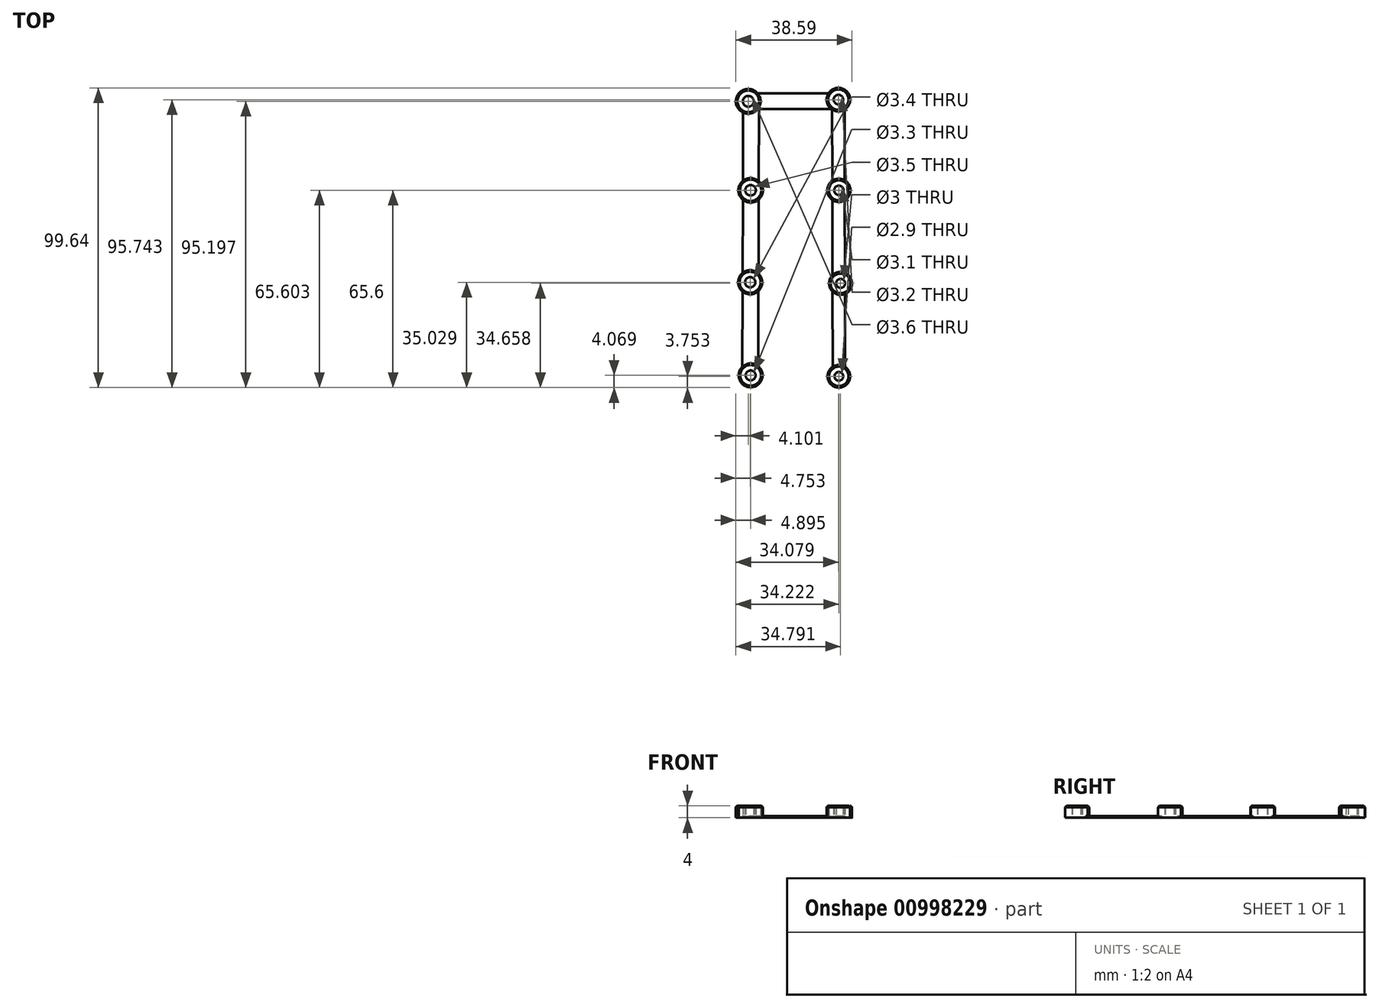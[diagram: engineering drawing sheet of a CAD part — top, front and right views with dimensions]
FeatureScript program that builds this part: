
annotation { "Feature Type Name" : "Feature", "Feature Type Description" : "" }
export const myFeature = defineFeature(function(context is Context, id is Id, definition is map)
    precondition{}
    {
        {
            var Q0;
            Q0=qCreatedBy(makeId("Top.planeOp"),FACE);
            var sketch = newSketch(context, id + "F0", { "sketchPlane" : qUnion([Q0])});
            skCircle(sketch, "E0", {"center": v(-37.62, 22.58) * mm, "radius": 4.1 * mm});
            skCircle(sketch, "E1", {"center": v(-36.82, -7.02) * mm, "radius": 4.05 * mm});
            skCircle(sketch, "E2", {"center": v(-36.97, -37.6) * mm, "radius": 4 * mm});
            skCircle(sketch, "E3", {"center": v(-36.83, -68.55) * mm, "radius": 3.95 * mm});
            skCircle(sketch, "E4", {"center": v(-7.64, 23.12) * mm, "radius": 3.9 * mm});
            skCircle(sketch, "E5", {"center": v(-7.5, -7.02) * mm, "radius": 3.85 * mm});
            skCircle(sketch, "E6", {"center": v(-6.93, -37.96) * mm, "radius": 3.8 * mm});
            skCircle(sketch, "E7", {"center": v(-7.5, -68.87) * mm, "radius": 3.75 * mm});
            skCircle(sketch, "E8", {"center": v(-37.62, 22.58) * mm, "radius": 1.8 * mm});
            skCircle(sketch, "E9", {"center": v(-36.82, -7.02) * mm, "radius": 1.75 * mm});
            skCircle(sketch, "E10", {"center": v(-36.97, -37.6) * mm, "radius": 1.7 * mm});
            skCircle(sketch, "E11", {"center": v(-36.83, -68.55) * mm, "radius": 1.65 * mm});
            skCircle(sketch, "E12", {"center": v(-7.64, 23.12) * mm, "radius": 1.6 * mm});
            skCircle(sketch, "E13", {"center": v(-7.5, -7.02) * mm, "radius": 1.55 * mm});
            skCircle(sketch, "E14", {"center": v(-6.93, -37.96) * mm, "radius": 1.5 * mm});
            skCircle(sketch, "E15", {"center": v(-7.5, -68.87) * mm, "radius": 1.45 * mm});
            skLineSegment(sketch, "E16.left", {"start": v(-39.32, 18.84) * mm, "end": v(-39.39, -3.88) * mm});
            skLineSegment(sketch, "E16.right", {"start": v(-34.03, 20.02) * mm, "end": v(-34.1, -4.01) * mm});
            skLineSegment(sketch, "E17.left", {"start": v(-9.72, 19.82) * mm, "end": v(-9.68, -3.85) * mm});
            skLineSegment(sketch, "E17.right", {"start": v(-5.6, 19.8) * mm, "end": v(-5.56, -3.7) * mm});
            skPoint(sketch, "E18.orphan", {"position": v(-34.33, -75.74) * mm});
            skPoint(sketch, "E19.orphan", {"position": v(-5.43, -75.74) * mm});
            skLineSegment(sketch, "E20.trimOffspring", {"start": v(-34.03, 20.02) * mm, "end": v(-10, 20.02) * mm});
            skLineSegment(sketch, "E21.trimOffspring", {"start": v(-34.45, 25.17) * mm, "end": v(-10.96, 25.17) * mm});
            skLineSegment(sketch, "E22.trimOffspring", {"start": v(-39.4, -10.14) * mm, "end": v(-39.48, -34.48) * mm});
            skLineSegment(sketch, "E23.trimOffspring", {"start": v(-34.13, -10.04) * mm, "end": v(-34.2, -34.7) * mm});
            skLineSegment(sketch, "E24.trimOffspring", {"start": v(-9.67, -10.2) * mm, "end": v(-9.62, -35.28) * mm});
            skLineSegment(sketch, "E25.trimOffspring", {"start": v(-5.54, -10.34) * mm, "end": v(-5.5, -34.44) * mm});
            skLineSegment(sketch, "E26.trimOffspring", {"start": v(-39.5, -40.69) * mm, "end": v(-39.58, -65.72) * mm});
            skLineSegment(sketch, "E27.trimOffspring", {"start": v(-34.22, -40.5) * mm, "end": v(-34.3, -65.52) * mm});
            skLineSegment(sketch, "E28.trimOffspring", {"start": v(-5.49, -41.48) * mm, "end": v(-5.45, -65.73) * mm});
            skLineSegment(sketch, "E29.trimOffspring", {"start": v(-9.61, -40.65) * mm, "end": v(-9.57, -65.74) * mm});
            skSolve(sketch);
        }
        {
            var Q0;
            Q0=makeQuery(id+"F0.imprint","IMPRINT",FACE,{"disambiguationData":[TD([[makeQuery(id+"F0.imprint","IMPRINT",EDGE,{"derivedFrom":sQuery(id+"F0.wireOp",EDGE,"E0")}),-1.0]])]});
            var Q1;
            {var subQ0=sQuery(id+"F0.wireOp",EDGE,"E16.left");var subQ1=sQuery(id+"F0.wireOp",EDGE,"E1");var subQ2=makeQuery(id+"F0.imprint","INTERSECT",VERTEX,{"disambiguationData":[OD(1.0)],"derivedFrom":[subQ1,subQ0]});Q1=makeQuery(id+"F0.imprint","IMPRINT",FACE,{"disambiguationData":[TD([[makeQuery(id+"F0.imprint","IMPRINT",EDGE,{"disambiguationData":[TD([[subQ2,-1.0]])],"derivedFrom":subQ1}),-1.0]])]});}
            var Q2;
            {var subQ0=sQuery(id+"F0.wireOp",EDGE,"E16.left");var subQ1=sQuery(id+"F0.wireOp",EDGE,"E2");var subQ2=makeQuery(id+"F0.imprint","INTERSECT",VERTEX,{"disambiguationData":[OD(1.0)],"derivedFrom":[subQ1,subQ0]});Q2=makeQuery(id+"F0.imprint","IMPRINT",FACE,{"disambiguationData":[TD([[makeQuery(id+"F0.imprint","IMPRINT",EDGE,{"disambiguationData":[TD([[subQ2,-1.0]])],"derivedFrom":subQ1}),-1.0]])]});}
            var Q3;
            {var subQ0=sQuery(id+"F0.wireOp",EDGE,"E17.left");var subQ1=sQuery(id+"F0.wireOp",EDGE,"E5");var subQ2=makeQuery(id+"F0.imprint","INTERSECT",VERTEX,{"disambiguationData":[OD(1.0)],"derivedFrom":[subQ1,subQ0]});Q3=makeQuery(id+"F0.imprint","IMPRINT",FACE,{"disambiguationData":[TD([[makeQuery(id+"F0.imprint","IMPRINT",EDGE,{"disambiguationData":[TD([[subQ2,-1.0]])],"derivedFrom":subQ1}),-1.0]])]});}
            var Q4;
            {var subQ0=sQuery(id+"F0.wireOp",EDGE,"E17.left");var subQ1=sQuery(id+"F0.wireOp",EDGE,"E6");var subQ2=makeQuery(id+"F0.imprint","INTERSECT",VERTEX,{"disambiguationData":[OD(1.0)],"derivedFrom":[subQ1,subQ0]});Q4=makeQuery(id+"F0.imprint","IMPRINT",FACE,{"disambiguationData":[TD([[makeQuery(id+"F0.imprint","IMPRINT",EDGE,{"disambiguationData":[TD([[subQ2,-1.0]])],"derivedFrom":subQ1}),-1.0]])]});}
            var Q5;
            {var subQ0=sQuery(id+"F0.wireOp",EDGE,"E16.left");var subQ5=sQuery(id+"F0.wireOp",EDGE,"E0");var subQ6=makeQuery(id+"F0.imprint","INTERSECT",VERTEX,{"derivedFrom":[subQ5,subQ0]});Q5=makeQuery(id+"F0.imprint","IMPRINT",FACE,{"disambiguationData":[TD([[makeQuery(id+"F0.imprint","IMPRINT",EDGE,{"disambiguationData":[TD([[subQ6,-1.0]])],"derivedFrom":subQ5}),-1.0]])]});}
            var Q6;
            {var subQ5=sQuery(id+"F0.wireOp",EDGE,"kUI5SBMI-iPfT-wOSN-fbtu-PMcIkSxUXb8U.left");Q6=makeQuery(id+"F0.imprint","IMPRINT",FACE,{"disambiguationData":[TD([[makeQuery(id+"F0.imprint","IMPRINT",EDGE,{"derivedFrom":subQ5}),1.0]])]});}
            var Q7;
            {var subQ0=sQuery(id+"F0.wireOp",EDGE,"kUI5SBMI-iPfT-wOSN-fbtu-PMcIkSxUXb8U.bottom");var subQ3=sQuery(id+"F0.wireOp",EDGE,"E4");var subQ4=makeQuery(id+"F0.imprint","INTERSECT",VERTEX,{"disambiguationData":[OD(0.0)],"derivedFrom":[subQ3,subQ0]});Q7=makeQuery(id+"F0.imprint","IMPRINT",FACE,{"disambiguationData":[TD([[makeQuery(id+"F0.imprint","IMPRINT",EDGE,{"disambiguationData":[TD([[subQ4,-1.0]])],"derivedFrom":subQ3}),-1.0]])]});}
            var Q8;
            {var subQ5=sQuery(id+"F0.wireOp",EDGE,"kUI5SBMI-iPfT-wOSN-fbtu-PMcIkSxUXb8U.right");Q8=makeQuery(id+"F0.imprint","IMPRINT",FACE,{"disambiguationData":[TD([[makeQuery(id+"F0.imprint","IMPRINT",EDGE,{"derivedFrom":subQ5}),-1.0]])]});}
            var Q9;
            {var subQ0=sQuery(id+"F0.wireOp",EDGE,"E17.left");var subQ1=sQuery(id+"F0.wireOp",EDGE,"E4");var subQ2=makeQuery(id+"F0.imprint","INTERSECT",VERTEX,{"derivedFrom":[subQ1,subQ0]});Q9=makeQuery(id+"F0.imprint","IMPRINT",FACE,{"disambiguationData":[TD([[makeQuery(id+"F0.imprint","IMPRINT",EDGE,{"disambiguationData":[TD([[subQ2,-1.0]])],"derivedFrom":subQ1}),-1.0]])]});}
            extrude(context, id + "F1", {"entities" : qUnion([Q0, Q1, Q2, Q3, Q4, Q5, Q6, Q7, Q8, Q9]), "depth" : .5 * mm, "offsetDistance" : 25 * mm});
        }
        {
            var Q0;
            Q0=makeQuery(id+"F0.imprint","IMPRINT",FACE,{"disambiguationData":[TD([[makeQuery(id+"F0.imprint","IMPRINT",EDGE,{"derivedFrom":sQuery(id+"F0.wireOp",EDGE,"E0")}),1.0]])]});
            var Q1;
            Q1=makeQuery(id+"F0.imprint","IMPRINT",FACE,{"disambiguationData":[TD([[makeQuery(id+"F0.imprint","IMPRINT",EDGE,{"derivedFrom":sQuery(id+"F0.wireOp",EDGE,"E1")}),1.0]])]});
            var Q2;
            Q2=makeQuery(id+"F0.imprint","IMPRINT",FACE,{"disambiguationData":[TD([[makeQuery(id+"F0.imprint","IMPRINT",EDGE,{"derivedFrom":sQuery(id+"F0.wireOp",EDGE,"E2")}),1.0]])]});
            var Q3;
            Q3=makeQuery(id+"F0.imprint","IMPRINT",FACE,{"disambiguationData":[TD([[makeQuery(id+"F0.imprint","IMPRINT",EDGE,{"derivedFrom":sQuery(id+"F0.wireOp",EDGE,"E3")}),1.0]])]});
            var Q4;
            Q4=makeQuery(id+"F0.imprint","IMPRINT",FACE,{"disambiguationData":[TD([[makeQuery(id+"F0.imprint","IMPRINT",EDGE,{"derivedFrom":sQuery(id+"F0.wireOp",EDGE,"E7")}),1.0]])]});
            var Q5;
            Q5=makeQuery(id+"F0.imprint","IMPRINT",FACE,{"disambiguationData":[TD([[makeQuery(id+"F0.imprint","IMPRINT",EDGE,{"derivedFrom":sQuery(id+"F0.wireOp",EDGE,"E6")}),1.0]])]});
            var Q6;
            Q6=makeQuery(id+"F0.imprint","IMPRINT",FACE,{"disambiguationData":[TD([[makeQuery(id+"F0.imprint","IMPRINT",EDGE,{"derivedFrom":sQuery(id+"F0.wireOp",EDGE,"E5")}),1.0]])]});
            var Q7;
            Q7=makeQuery(id+"F0.imprint","IMPRINT",FACE,{"disambiguationData":[TD([[makeQuery(id+"F0.imprint","IMPRINT",EDGE,{"derivedFrom":sQuery(id+"F0.wireOp",EDGE,"E4")}),1.0]])]});
            var Q8;
            {var subQ0=sQuery(id+"F0.wireOp",EDGE,"E16.left");var subQ1=sQuery(id+"F0.wireOp",EDGE,"E1");var subQ2=makeQuery(id+"F0.imprint","INTERSECT",VERTEX,{"disambiguationData":[OD(0.0)],"derivedFrom":[subQ1,subQ0]});Q8=makeQuery(id+"F0.imprint","IMPRINT",FACE,{"disambiguationData":[TD([[makeQuery(id+"F0.imprint","IMPRINT",EDGE,{"disambiguationData":[TD([[subQ2,-1.0]])],"derivedFrom":subQ1}),1.0]])]});}
            var Q9;
            {var subQ0=sQuery(id+"F0.wireOp",EDGE,"E16.right");var subQ1=sQuery(id+"F0.wireOp",EDGE,"E1");var subQ2=makeQuery(id+"F0.imprint","INTERSECT",VERTEX,{"disambiguationData":[OD(0.0)],"derivedFrom":[subQ1,subQ0]});Q9=makeQuery(id+"F0.imprint","IMPRINT",FACE,{"disambiguationData":[TD([[makeQuery(id+"F0.imprint","IMPRINT",EDGE,{"disambiguationData":[TD([[subQ2,1.0]])],"derivedFrom":subQ1}),1.0]])]});}
            var Q10;
            {var subQ0=sQuery(id+"F0.wireOp",EDGE,"E16.left");var subQ1=sQuery(id+"F0.wireOp",EDGE,"E2");var subQ2=makeQuery(id+"F0.imprint","INTERSECT",VERTEX,{"disambiguationData":[OD(0.0)],"derivedFrom":[subQ1,subQ0]});Q10=makeQuery(id+"F0.imprint","IMPRINT",FACE,{"disambiguationData":[TD([[makeQuery(id+"F0.imprint","IMPRINT",EDGE,{"disambiguationData":[TD([[subQ2,-1.0]])],"derivedFrom":subQ1}),1.0]])]});}
            var Q11;
            {var subQ0=sQuery(id+"F0.wireOp",EDGE,"E16.right");var subQ1=sQuery(id+"F0.wireOp",EDGE,"E2");var subQ2=makeQuery(id+"F0.imprint","INTERSECT",VERTEX,{"disambiguationData":[OD(0.0)],"derivedFrom":[subQ1,subQ0]});Q11=makeQuery(id+"F0.imprint","IMPRINT",FACE,{"disambiguationData":[TD([[makeQuery(id+"F0.imprint","IMPRINT",EDGE,{"disambiguationData":[TD([[subQ2,1.0]])],"derivedFrom":subQ1}),1.0]])]});}
            var Q12;
            {var subQ0=sQuery(id+"F0.wireOp",EDGE,"E17.left");var subQ1=sQuery(id+"F0.wireOp",EDGE,"E5");var subQ2=makeQuery(id+"F0.imprint","INTERSECT",VERTEX,{"disambiguationData":[OD(0.0)],"derivedFrom":[subQ1,subQ0]});Q12=makeQuery(id+"F0.imprint","IMPRINT",FACE,{"disambiguationData":[TD([[makeQuery(id+"F0.imprint","IMPRINT",EDGE,{"disambiguationData":[TD([[subQ2,-1.0]])],"derivedFrom":subQ1}),1.0]])]});}
            var Q13;
            {var subQ0=sQuery(id+"F0.wireOp",EDGE,"E17.right");var subQ1=sQuery(id+"F0.wireOp",EDGE,"E5");var subQ2=makeQuery(id+"F0.imprint","INTERSECT",VERTEX,{"disambiguationData":[OD(0.0)],"derivedFrom":[subQ1,subQ0]});Q13=makeQuery(id+"F0.imprint","IMPRINT",FACE,{"disambiguationData":[TD([[makeQuery(id+"F0.imprint","IMPRINT",EDGE,{"disambiguationData":[TD([[subQ2,1.0]])],"derivedFrom":subQ1}),1.0]])]});}
            var Q14;
            {var subQ0=sQuery(id+"F0.wireOp",EDGE,"E17.left");var subQ1=sQuery(id+"F0.wireOp",EDGE,"E6");var subQ2=makeQuery(id+"F0.imprint","INTERSECT",VERTEX,{"disambiguationData":[OD(0.0)],"derivedFrom":[subQ1,subQ0]});Q14=makeQuery(id+"F0.imprint","IMPRINT",FACE,{"disambiguationData":[TD([[makeQuery(id+"F0.imprint","IMPRINT",EDGE,{"disambiguationData":[TD([[subQ2,-1.0]])],"derivedFrom":subQ1}),1.0]])]});}
            var Q15;
            {var subQ0=sQuery(id+"F0.wireOp",EDGE,"E17.right");var subQ1=sQuery(id+"F0.wireOp",EDGE,"E6");var subQ2=makeQuery(id+"F0.imprint","INTERSECT",VERTEX,{"disambiguationData":[OD(0.0)],"derivedFrom":[subQ1,subQ0]});Q15=makeQuery(id+"F0.imprint","IMPRINT",FACE,{"disambiguationData":[TD([[makeQuery(id+"F0.imprint","IMPRINT",EDGE,{"disambiguationData":[TD([[subQ2,1.0]])],"derivedFrom":subQ1}),1.0]])]});}
            var Q16;
            {var subQ0=sQuery(id+"F0.wireOp",EDGE,"E16.right");var subQ1=sQuery(id+"F0.wireOp",EDGE,"E3");var subQ2=makeQuery(id+"F0.imprint","INTERSECT",VERTEX,{"disambiguationData":[OD(0.0)],"derivedFrom":[subQ1,subQ0]});Q16=makeQuery(id+"F0.imprint","IMPRINT",FACE,{"disambiguationData":[TD([[makeQuery(id+"F0.imprint","IMPRINT",EDGE,{"disambiguationData":[TD([[subQ2,-1.0]])],"derivedFrom":subQ1}),1.0]])]});}
            var Q17;
            {var subQ0=sQuery(id+"F0.wireOp",EDGE,"E16.left");var subQ1=sQuery(id+"F0.wireOp",EDGE,"E3");var subQ2=makeQuery(id+"F0.imprint","INTERSECT",VERTEX,{"disambiguationData":[OD(0.0)],"derivedFrom":[subQ1,subQ0]});Q17=makeQuery(id+"F0.imprint","IMPRINT",FACE,{"disambiguationData":[TD([[makeQuery(id+"F0.imprint","IMPRINT",EDGE,{"disambiguationData":[TD([[subQ2,1.0]])],"derivedFrom":subQ1}),1.0]])]});}
            var Q18;
            {var subQ0=sQuery(id+"F0.wireOp",EDGE,"E17.left");var subQ1=sQuery(id+"F0.wireOp",EDGE,"E7");var subQ2=makeQuery(id+"F0.imprint","INTERSECT",VERTEX,{"disambiguationData":[OD(0.0)],"derivedFrom":[subQ1,subQ0]});Q18=makeQuery(id+"F0.imprint","IMPRINT",FACE,{"disambiguationData":[TD([[makeQuery(id+"F0.imprint","IMPRINT",EDGE,{"disambiguationData":[TD([[subQ2,1.0]])],"derivedFrom":subQ1}),1.0]])]});}
            var Q19;
            {var subQ0=sQuery(id+"F0.wireOp",EDGE,"E17.right");var subQ1=sQuery(id+"F0.wireOp",EDGE,"E7");var subQ2=makeQuery(id+"F0.imprint","INTERSECT",VERTEX,{"disambiguationData":[OD(0.0)],"derivedFrom":[subQ1,subQ0]});Q19=makeQuery(id+"F0.imprint","IMPRINT",FACE,{"disambiguationData":[TD([[makeQuery(id+"F0.imprint","IMPRINT",EDGE,{"disambiguationData":[TD([[subQ2,-1.0]])],"derivedFrom":subQ1}),1.0]])]});}
            extrude(context, id + "F2", {"entities" : qUnion([Q0, Q1, Q2, Q3, Q4, Q5, Q6, Q7, Q8, Q9, Q10, Q11, Q12, Q13, Q14, Q15, Q16, Q17, Q18, Q19]), "operationType" : NewBodyOperationType.ADD, "depth" : 4 * mm, "offsetDistance" : 25 * mm});
        }
        {
            var Q0;
            Q0=makeQuery(id+"F2.opExtrude","CAP_EDGE",EDGE,{"disambiguationData":[OSD([sQuery(id+"F0.wireOp",EDGE,"E0")])],"isStart":false});
            var Q1;
            Q1=makeQuery(id+"F2.opExtrude","CAP_EDGE",EDGE,{"disambiguationData":[OSD([sQuery(id+"F0.wireOp",EDGE,"E1")])],"isStart":false});
            var Q2;
            Q2=makeQuery(id+"F2.opExtrude","CAP_EDGE",EDGE,{"disambiguationData":[OSD([sQuery(id+"F0.wireOp",EDGE,"E2")])],"isStart":false});
            var Q3;
            Q3=makeQuery(id+"F2.opExtrude","CAP_EDGE",EDGE,{"disambiguationData":[OSD([sQuery(id+"F0.wireOp",EDGE,"E3")])],"isStart":false});
            var Q4;
            Q4=makeQuery(id+"F2.opExtrude","CAP_EDGE",EDGE,{"disambiguationData":[OSD([sQuery(id+"F0.wireOp",EDGE,"E4")])],"isStart":false});
            var Q5;
            Q5=makeQuery(id+"F2.opExtrude","CAP_EDGE",EDGE,{"disambiguationData":[OSD([sQuery(id+"F0.wireOp",EDGE,"E5")])],"isStart":false});
            var Q6;
            Q6=makeQuery(id+"F2.opExtrude","CAP_EDGE",EDGE,{"disambiguationData":[OSD([sQuery(id+"F0.wireOp",EDGE,"E6")])],"isStart":false});
            var Q7;
            Q7=makeQuery(id+"F2.opExtrude","CAP_EDGE",EDGE,{"disambiguationData":[OSD([sQuery(id+"F0.wireOp",EDGE,"E7")])],"isStart":false});
            chamfer(context, id + "F3", {"entities" : qUnion([Q0, Q1, Q2, Q3, Q4, Q5, Q6, Q7]), "width" : .5 * mm, "tangentPropagation" : true});
        }
    });
